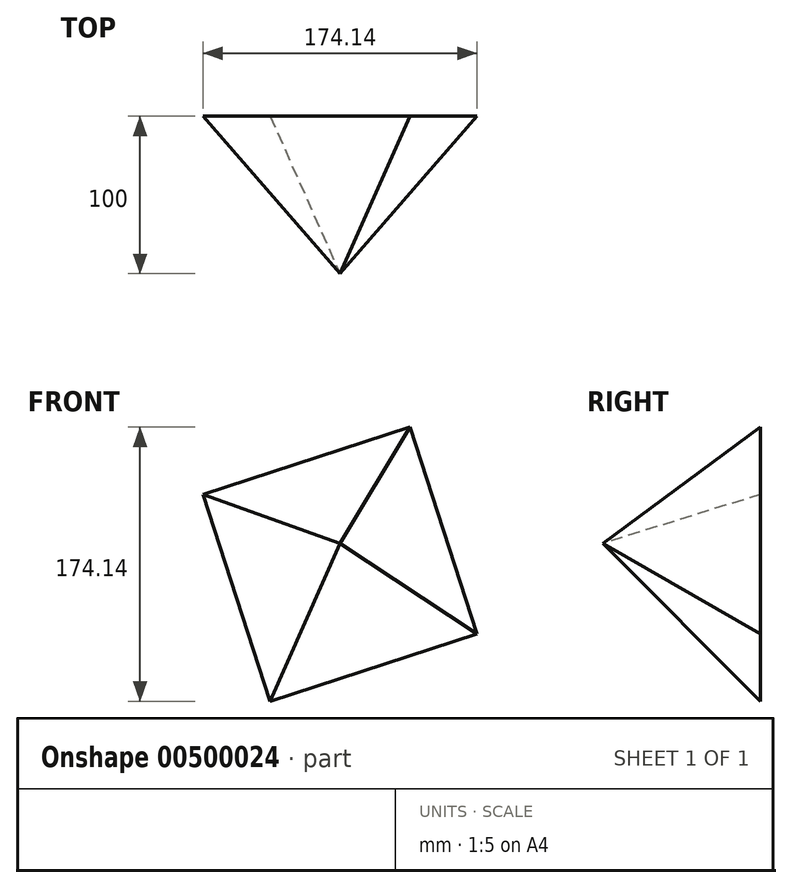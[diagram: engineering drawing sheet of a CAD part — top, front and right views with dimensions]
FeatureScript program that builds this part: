
annotation { "Feature Type Name" : "Feature", "Feature Type Description" : "" }
export const myFeature = defineFeature(function(context is Context, id is Id, definition is map)
    precondition{}
    {
        {
            var Q0;
            Q0=qCreatedBy(makeId("Front.planeOp"),FACE);
            var sketch = newSketch(context, id + "F0", { "sketchPlane" : qUnion([Q0])});
            skCircle(sketch, "E0.cCircle", {"center": v(0, 0) * mm, "radius": 97.7 * mm, "construction": true});
            skLineSegment(sketch, "E0.0", {"start": v(-87.07, 44.32) * mm, "end": v(44.32, 87.07) * mm});
            skLineSegment(sketch, "E0.1", {"start": v(44.32, 87.07) * mm, "end": v(87.07, -44.32) * mm});
            skLineSegment(sketch, "E0.2", {"start": v(87.07, -44.32) * mm, "end": v(-44.32, -87.07) * mm});
            skLineSegment(sketch, "E0.3", {"start": v(-44.32, -87.07) * mm, "end": v(-87.07, 44.32) * mm});
            skSolve(sketch);
        }
        {
            var Q0;
            Q0=qCreatedBy(makeId("Front.planeOp"),FACE);
            cPlane(context, id + "F1", {"entities" : qUnion([Q0]), "cplaneType" : CPlaneType.OFFSET, "offset" : 100 * mm, "width" : 150 * mm, "height" : 150 * mm});
        }
        {
            var Q0;
            Q0=qCreatedBy(id+"F1.planeOp",FACE);
            var sketch = newSketch(context, id + "F2", { "sketchPlane" : qUnion([Q0])});
            skPoint(sketch, "E1", {"position": v(0, 13.22) * mm});
            skSolve(sketch);
        }
        {
            var Q0;
            Q0=makeQuery(id+"F0.imprint","IMPRINT",FACE,{"disambiguationData":[TD([[makeQuery(id+"F0.imprint","IMPRINT",EDGE,{"derivedFrom":sQuery(id+"F0.wireOp",EDGE,"E0.0")}),-1.0]])]});
            var Q1;
            Q1=sQuery(id+"F2.wireOp",VERTEX,"E1");
            loft(context, id + "F3", {"sheetProfilesArray" : [{ "sheetProfileEntities" : qUnion([Q0]) }, { "sheetProfileEntities" : qUnion([Q1]) }]});
        }
    });
